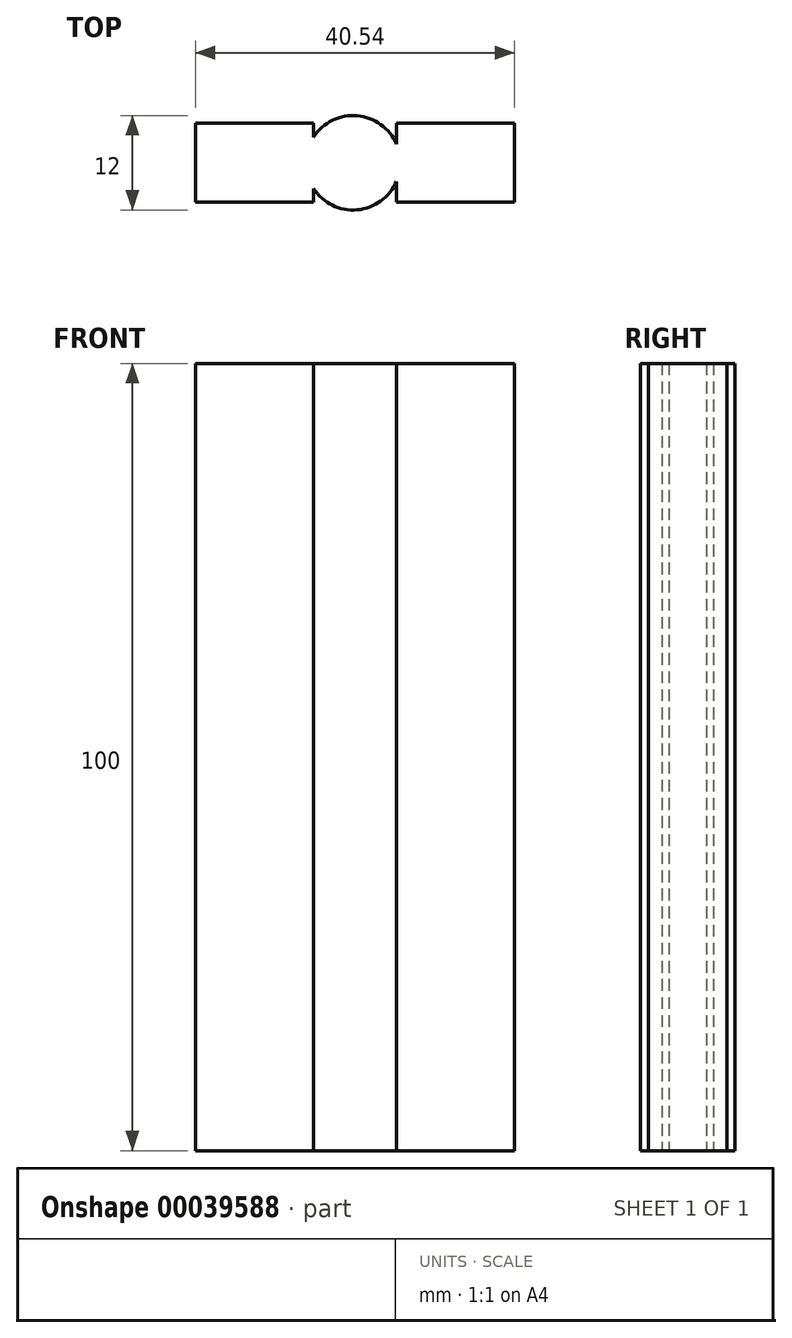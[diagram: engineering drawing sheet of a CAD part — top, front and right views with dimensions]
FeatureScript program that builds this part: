
annotation { "Feature Type Name" : "Feature", "Feature Type Description" : "" }
export const myFeature = defineFeature(function(context is Context, id is Id, definition is map)
    precondition{}
    {
        {
            var Q0;
            Q0=qCreatedBy(makeId("Top.planeOp"),FACE);
            var sketch = newSketch(context, id + "F0", { "sketchPlane" : qUnion([Q0])});
            skCircle(sketch, "E0", {"center": v(0, 0) * mm, "radius": 6 * mm});
            skSolve(sketch);
        }
        {
            var Q0;
            Q0 = qSketchRegion(id + "F0", true);
            extrude(context, id + "F1", {"entities" : qUnion([Q0]), "depth" : 100 * mm});
        }
        {
            var Q0;
            Q0=qCreatedBy(makeId("Front.planeOp"),FACE);
            var sketch = newSketch(context, id + "F2", { "sketchPlane" : qUnion([Q0])});
            skLineSegment(sketch, "E1.bottom", {"start": v(-5.03, 100) * mm, "end": v(-20.03, 100) * mm});
            skLineSegment(sketch, "E1.top", {"start": v(-5.03, 0) * mm, "end": v(-20.03, 0) * mm});
            skLineSegment(sketch, "E1.left", {"start": v(-5.03, 100) * mm, "end": v(-5.03, 0) * mm});
            skLineSegment(sketch, "E1.right", {"start": v(-20.03, 100) * mm, "end": v(-20.03, 0) * mm});
            skSolve(sketch);
        }
        {
            var Q0;
            Q0 = qSketchRegion(id + "F2", true);
            extrude(context, id + "F3", {"entities" : qUnion([Q0]), "operationType" : NewBodyOperationType.ADD, "endBound" : BoundingType.SYMMETRIC, "depth" : 10 * mm});
        }
        {
            var Q0;
            Q0=qCreatedBy(makeId("Front.planeOp"),FACE);
            var sketch = newSketch(context, id + "F4", { "sketchPlane" : qUnion([Q0])});
            skLineSegment(sketch, "E2.bottom", {"start": v(5.51, 0) * mm, "end": v(20.51, 0) * mm});
            skLineSegment(sketch, "E2.top", {"start": v(5.51, 100) * mm, "end": v(20.51, 100) * mm});
            skLineSegment(sketch, "E2.left", {"start": v(5.51, 0) * mm, "end": v(5.51, 100) * mm});
            skLineSegment(sketch, "E2.right", {"start": v(20.51, 0) * mm, "end": v(20.51, 100) * mm});
            skSolve(sketch);
        }
        {
            var Q0;
            Q0=makeQuery(id+"F4.imprint","IMPRINT",FACE,{"disambiguationData":[TD([[makeQuery(id+"F4.imprint","IMPRINT",EDGE,{"derivedFrom":sQuery(id+"F4.wireOp",EDGE,"E2.bottom")}),1.0]])]});
            extrude(context, id + "F5", {"entities" : qUnion([Q0]), "operationType" : NewBodyOperationType.ADD, "endBound" : BoundingType.SYMMETRIC, "depth" : 10 * mm});
        }
    });
